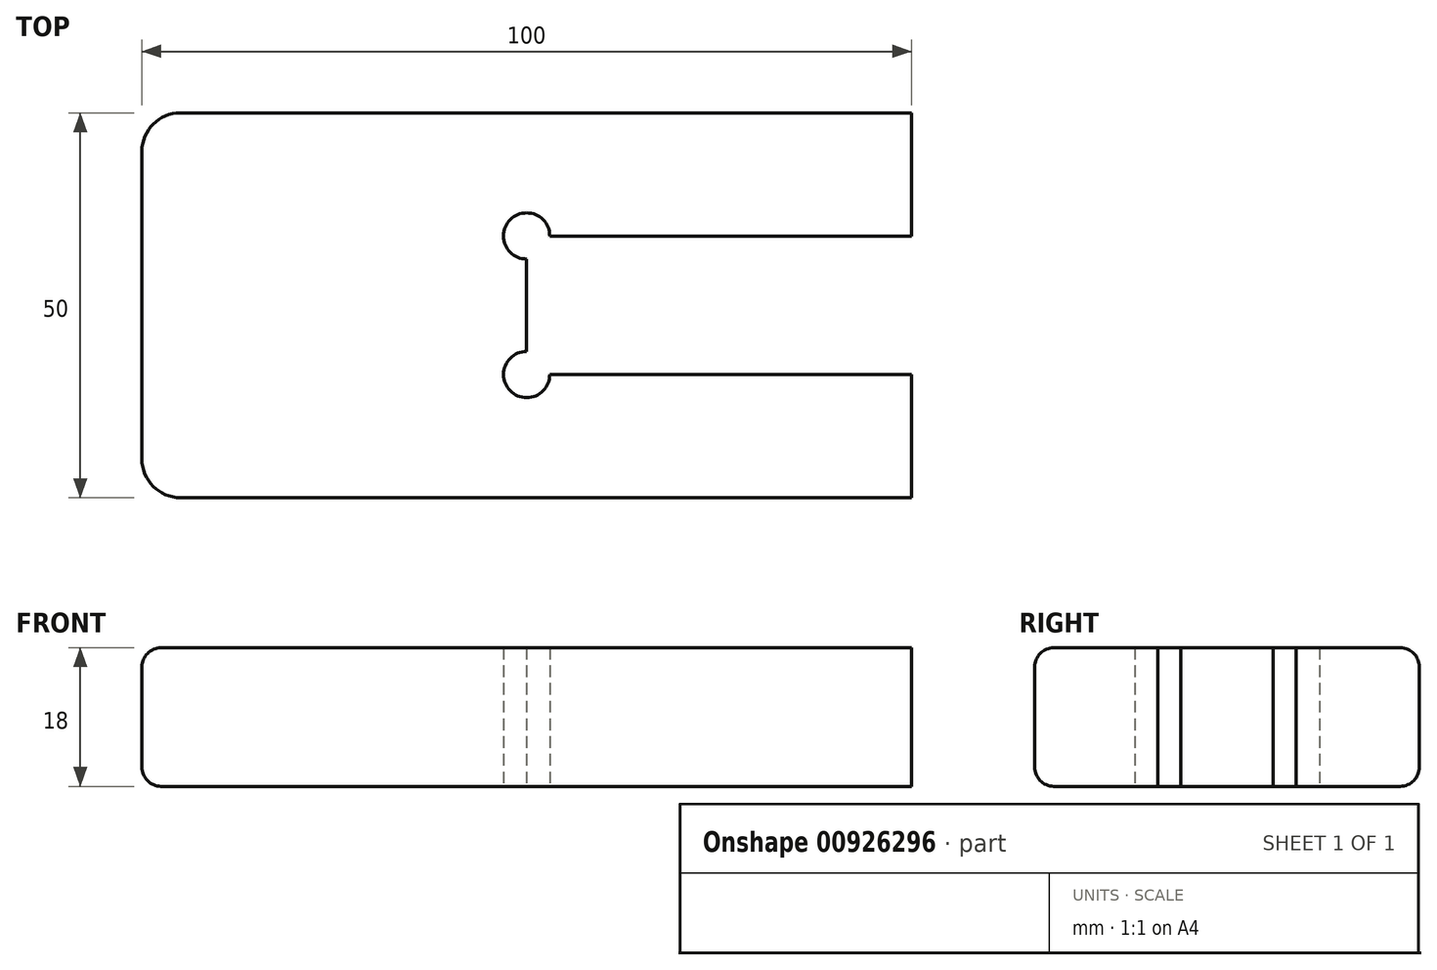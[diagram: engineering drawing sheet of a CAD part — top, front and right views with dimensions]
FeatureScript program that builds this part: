
annotation { "Feature Type Name" : "Feature", "Feature Type Description" : "" }
export const myFeature = defineFeature(function(context is Context, id is Id, definition is map)
    precondition{}
    {
        {
            var Q0;
            Q0=qCreatedBy(makeId("Top.planeOp"),FACE);
            var sketch = newSketch(context, id + "F0", { "sketchPlane" : qUnion([Q0])});
            skLineSegment(sketch, "E0", {"start": v(0, 0) * mm, "end": v(0, 50) * mm});
            skLineSegment(sketch, "E1", {"start": v(0, 50) * mm, "end": v(100, 50) * mm});
            skLineSegment(sketch, "E2", {"start": v(0, 0) * mm, "end": v(100, 0) * mm});
            skLineSegment(sketch, "E3", {"start": v(100, 0) * mm, "end": v(100, 16) * mm});
            skLineSegment(sketch, "E4", {"start": v(100, 50) * mm, "end": v(100, 34) * mm});
            skLineSegment(sketch, "E5", {"start": v(100, 34) * mm, "end": v(50, 34) * mm});
            skLineSegment(sketch, "E6", {"start": v(50, 34) * mm, "end": v(50, 16) * mm});
            skLineSegment(sketch, "E7", {"start": v(50, 16) * mm, "end": v(100, 16) * mm});
            skCircle(sketch, "E8", {"center": v(50, 34) * mm, "radius": 3 * mm});
            skCircle(sketch, "E9", {"center": v(50, 16) * mm, "radius": 3 * mm});
            skSolve(sketch);
        }
        {
            var Q0;
            Q0=makeQuery(id+"F0.imprint","IMPRINT",FACE,{"disambiguationData":[TD([[makeQuery(id+"F0.imprint","IMPRINT",EDGE,{"derivedFrom":sQuery(id+"F0.wireOp",EDGE,"E0")}),-1.0]])]});
            extrude(context, id + "F1", {"entities" : qUnion([Q0]), "depth" : 18 * mm, "offsetDistance" : 25 * mm});
        }
        {
            var Q0;
            Q0=makeQuery(id+"F1.opExtrude","SWEPT_EDGE",EDGE,{"disambiguationData":[OSD([sQuery(id+"F0.wireOp",EDGE,"E0"),sQuery(id+"F0.wireOp",EDGE,"E2")])]});
            var Q1;
            Q1=makeQuery(id+"F1.opExtrude","SWEPT_EDGE",EDGE,{"disambiguationData":[OSD([sQuery(id+"F0.wireOp",EDGE,"E0"),sQuery(id+"F0.wireOp",EDGE,"E1")])]});
            fillet(context, id + "F2", {"entities" : qUnion([Q0, Q1]), "radius" : 5 * mm, "tangentPropagation" : true, "allowEdgeOverflow" : false});
        }
        {
            var Q0;
            Q0=makeQuery(id+"F1.opExtrude","CAP_EDGE",EDGE,{"disambiguationData":[OSD([sQuery(id+"F0.wireOp",EDGE,"E2")])],"isStart":false});
            var Q1;
            Q1=makeQuery(id+"F1.opExtrude","CAP_EDGE",EDGE,{"disambiguationData":[OSD([sQuery(id+"F0.wireOp",EDGE,"E2")])],"isStart":true});
            fillet(context, id + "F3", {"entities" : qUnion([Q0, Q1]), "radius" : 2.5 * mm, "tangentPropagation" : true, "allowEdgeOverflow" : false});
        }
    });
